# Revit family: Circuit-Breakers_ABB_ReliaMod-EUSERC-Main-Fusible-Switch-600A
name_source: partatom
category: Electrical Equipment
units: mm (PartAtom-declared; Revit-internal decimal feet)

## family parameters
Cut with Voids When Loaded = No
Host = Face
OmniClass Number = 23.35.29.11
Panel Configuration = Two Columns, Circuits Across
Part Type = Panelboard
Room Calculation Point = No
Round Connector Dimension = Use Diameter
Shared = No

## types (2) — shared parameters
Apparent Load = 0 VA
Date Updated = 2023/08/07
Default Elevation = 4' - 0"
Enclosure = N3R Outdoor
Feed location = Bottom w/Integral Pullbox
Frames = XT6S
Fuse Type = Class T (Fuses not included)
ICRating = 100
Main amperage = 600 A
Main module type = EUSERC-Switch
Manufacturer = ABB
Primary material = ABB - Steel - White
Product data url = https://www.bimobject.com
URL = https://new.abb.com
Version = 1
zero-valued in all types: Power Factor

## per-type parameters (varying)
| type | Description | Number of Poles | Phase | Voltage | Voltage (V) |
| RMM1FE6RCLL | RELIAMOD 1PH 600A 100K EUSERC T MFS+PB | 2 | 1-Phase 3-Wire | 120/240V | 120 V |
| RMM3FE6RCLL | RELIAMOD 3PH 600A 100K EUSERC T MFS+PB | 3 | 3-Phase 4-Wire | 208Y/120V | 208 V |

note: column(s) folded — value = type name in every type: Model

## geometry (parser evidence)
native form markers: Sweep x20
no freeform markers — native parametric forms only
